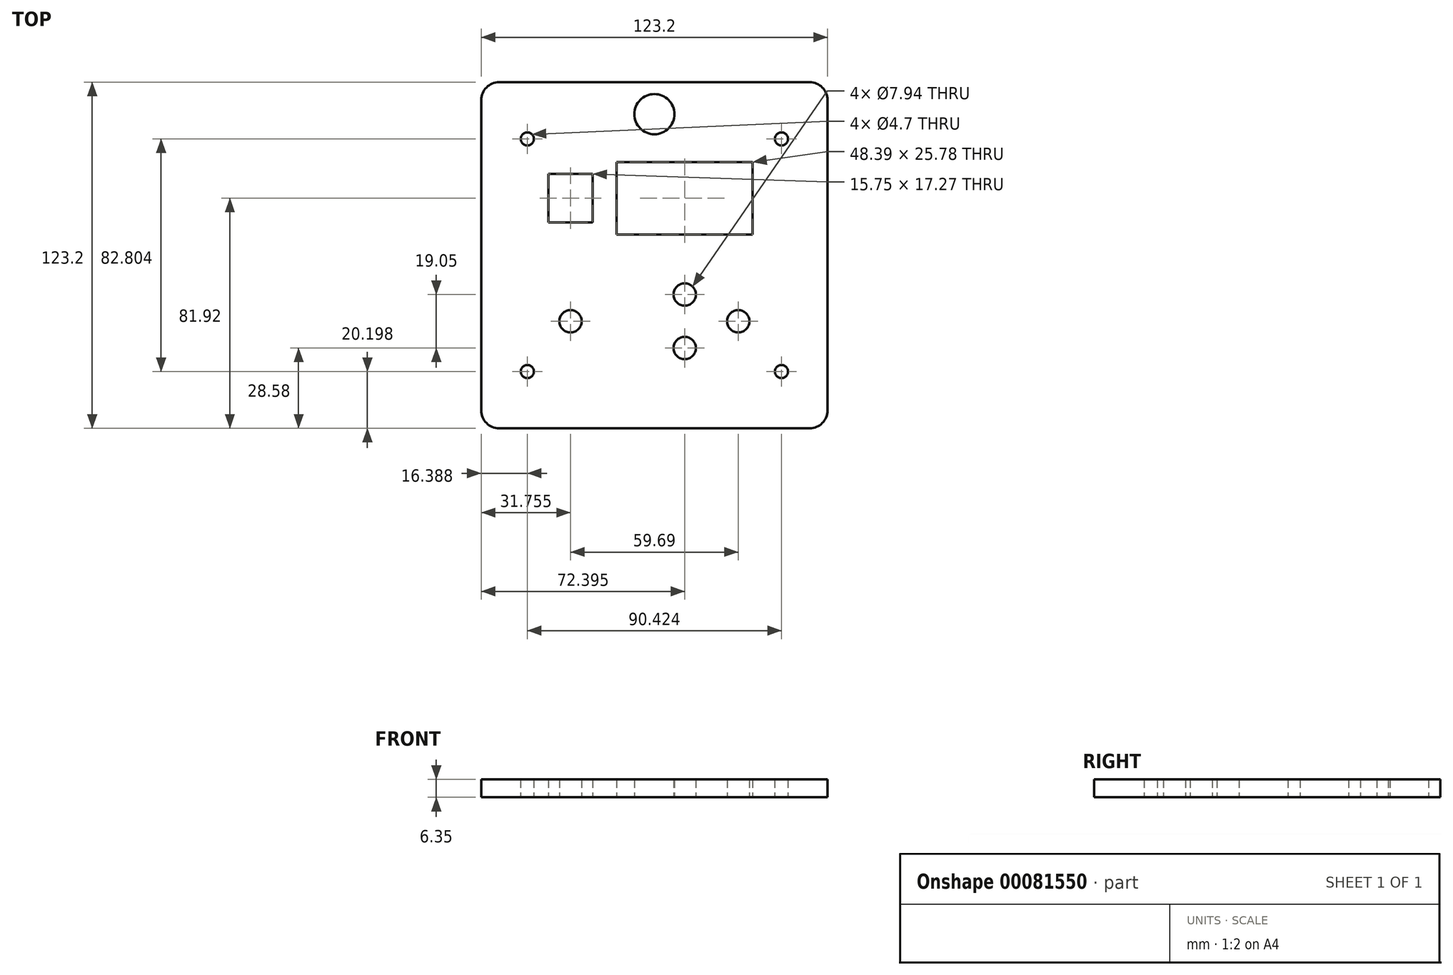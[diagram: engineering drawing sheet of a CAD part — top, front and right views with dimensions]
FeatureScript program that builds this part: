
annotation { "Feature Type Name" : "Feature", "Feature Type Description" : "" }
export const myFeature = defineFeature(function(context is Context, id is Id, definition is map)
    precondition{}
    {
        {
            var Q0;
            Q0=qCreatedBy(makeId("Top.planeOp"),FACE);
            var sketch = newSketch(context, id + "F0", { "sketchPlane" : qUnion([Q0])});
            skLineSegment(sketch, "E0.bottom", {"start": v(55.24, 61.6) * mm, "end": v(-55.25, 61.6) * mm});
            skLineSegment(sketch, "E0.top", {"start": v(55.25, -61.6) * mm, "end": v(-55.24, -61.6) * mm});
            skLineSegment(sketch, "E0.left", {"start": v(61.6, 55.25) * mm, "end": v(61.6, -55.25) * mm});
            skLineSegment(sketch, "E0.right", {"start": v(-61.6, 55.25) * mm, "end": v(-61.6, -55.25) * mm});
            skPoint(sketch, "E0.middle", {"position": v(0, 0) * mm});
            skPoint(sketch, "E1.visualSharp", {"position": v(-61.6, 61.6) * mm});
            skArc(sketch, "E1.filletArc", {"start": v(-55.25, 61.6) * mm, "mid": v(-59.74, 59.74) * mm, "end": v(-61.6, 55.25) * mm});
            skPoint(sketch, "E2.visualSharp", {"position": v(61.6, 61.6) * mm});
            skArc(sketch, "E2.filletArc", {"start": v(61.6, 55.25) * mm, "mid": v(59.74, 59.74) * mm, "end": v(55.24, 61.6) * mm});
            skPoint(sketch, "E3.visualSharp", {"position": v(-61.6, -61.6) * mm});
            skArc(sketch, "E3.filletArc", {"start": v(-61.6, -55.25) * mm, "mid": v(-59.74, -59.74) * mm, "end": v(-55.24, -61.6) * mm});
            skPoint(sketch, "E4.visualSharp", {"position": v(61.6, -61.6) * mm});
            skArc(sketch, "E4.filletArc", {"start": v(55.25, -61.6) * mm, "mid": v(59.74, -59.74) * mm, "end": v(61.6, -55.25) * mm});
            skLineSegment(sketch, "E5.bottom", {"start": v(34.99, 33.21) * mm, "end": v(-13.4, 33.21) * mm});
            skLineSegment(sketch, "E5.top", {"start": v(34.99, 7.43) * mm, "end": v(-13.4, 7.43) * mm});
            skLineSegment(sketch, "E5.left", {"start": v(34.99, 33.21) * mm, "end": v(34.99, 7.43) * mm});
            skLineSegment(sketch, "E5.right", {"start": v(-13.4, 33.21) * mm, "end": v(-13.4, 7.43) * mm});
            skPoint(sketch, "E5.middle", {"position": v(10.8, 20.32) * mm});
            skCircle(sketch, "E6", {"center": v(-29.84, -23.5) * mm, "radius": 3.97 * mm});
            skCircle(sketch, "E7", {"center": v(29.85, -23.5) * mm, "radius": 3.97 * mm});
            skCircle(sketch, "E8", {"center": v(10.8, -13.97) * mm, "radius": 3.97 * mm});
            skCircle(sketch, "E9", {"center": v(10.8, -33.02) * mm, "radius": 3.97 * mm});
            skLineSegment(sketch, "E10.bottom", {"start": v(-21.97, 28.96) * mm, "end": v(-37.72, 28.96) * mm});
            skLineSegment(sketch, "E10.top", {"start": v(-21.97, 11.68) * mm, "end": v(-37.72, 11.68) * mm});
            skLineSegment(sketch, "E10.left", {"start": v(-21.97, 28.96) * mm, "end": v(-21.97, 11.68) * mm});
            skLineSegment(sketch, "E10.right", {"start": v(-37.72, 28.96) * mm, "end": v(-37.72, 11.68) * mm});
            skPoint(sketch, "E10.middle", {"position": v(-29.84, 20.32) * mm});
            skLineSegment(sketch, "E11", {"start": v(-61.6, -23.5) * mm, "end": v(61.6, -23.5) * mm, "construction": true});
            skLineSegment(sketch, "E12", {"start": v(-29.85, 61.6) * mm, "end": v(-29.84, -61.6) * mm, "construction": true});
            skLineSegment(sketch, "E13", {"start": v(29.85, 61.6) * mm, "end": v(29.85, -61.6) * mm, "construction": true});
            skLineSegment(sketch, "E14", {"start": v(10.8, 61.6) * mm, "end": v(10.8, -61.6) * mm, "construction": true});
            skLineSegment(sketch, "E15", {"start": v(-61.6, -13.97) * mm, "end": v(61.6, -13.97) * mm, "construction": true});
            skCircle(sketch, "E16", {"center": v(0, 50.22) * mm, "radius": 7.14 * mm});
            skCircle(sketch, "E17", {"center": v(-45.21, 41.4) * mm, "radius": 2.35 * mm});
            skCircle(sketch, "E18.0.1.0", {"center": v(-45.21, -41.4) * mm, "radius": 2.35 * mm});
            skCircle(sketch, "E18.1.0.0", {"center": v(45.21, 41.4) * mm, "radius": 2.35 * mm});
            skCircle(sketch, "E18.1.1.0", {"center": v(45.21, -41.4) * mm, "radius": 2.35 * mm});
            skLineSegment(sketch, "E18.direction1", {"start": v(-45.21, 41.4) * mm, "end": v(45.21, 41.4) * mm, "construction": true});
            skLineSegment(sketch, "E18.direction2", {"start": v(-45.21, 41.4) * mm, "end": v(-45.21, -41.4) * mm, "construction": true});
            skSolve(sketch);
        }
        {
            var Q0;
            Q0 = qSketchRegion(id + "F0", true);
            extrude(context, id + "F1", {"entities" : qUnion([Q0]), "depth" : 6.35 * mm});
        }
    });
